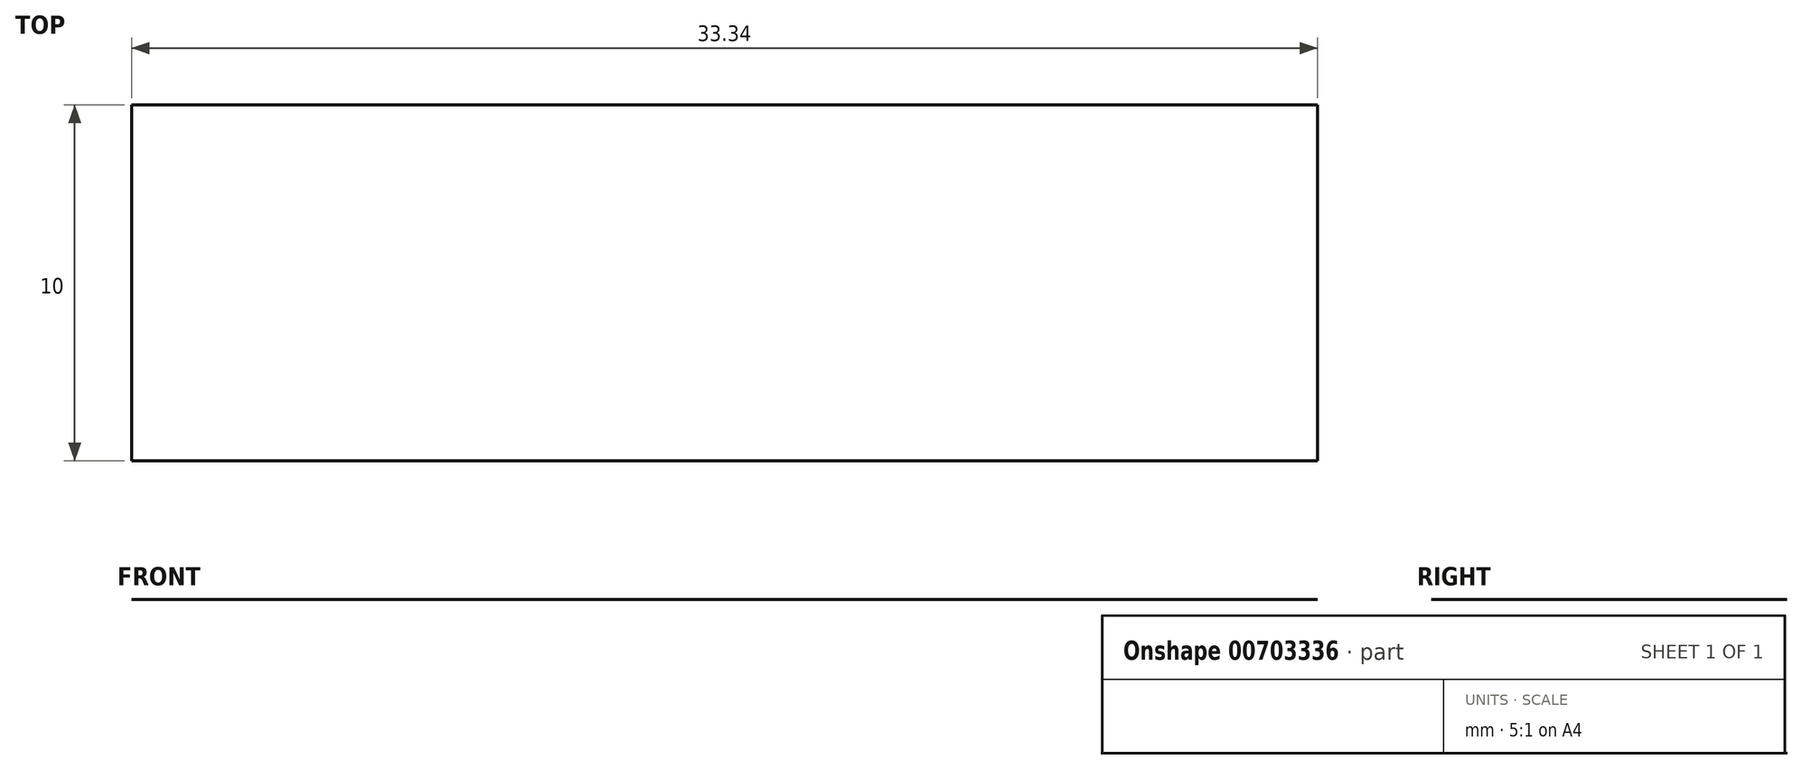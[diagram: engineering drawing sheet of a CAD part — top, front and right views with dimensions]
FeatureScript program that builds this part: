
annotation { "Feature Type Name" : "Feature", "Feature Type Description" : "" }
export const myFeature = defineFeature(function(context is Context, id is Id, definition is map)
    precondition{}
    {
        {
            var Q0;
            Q0=qCreatedBy(makeId("Top.planeOp"),FACE);
            var sketch = newSketch(context, id + "F0", { "sketchPlane" : qUnion([Q0])});
            skLineSegment(sketch, "E0.bottom", {"start": v(16.67, 5) * mm, "end": v(-16.67, 5) * mm});
            skLineSegment(sketch, "E0.top", {"start": v(16.67, -5) * mm, "end": v(-16.67, -5) * mm});
            skLineSegment(sketch, "E0.left", {"start": v(16.67, 5) * mm, "end": v(16.67, -5) * mm});
            skLineSegment(sketch, "E0.right", {"start": v(-16.67, 5) * mm, "end": v(-16.67, -5) * mm});
            skPoint(sketch, "E0.middle", {"position": v(0, 0) * mm});
            skSolve(sketch);
        }
        {
            var Q0;
            Q0 = qSketchRegion(id + "F0", true);
            extrude(context, id + "F1", {"entities" : qUnion([Q0]), "depth" : 1 / 406.4 * mm, "offsetDistance" : 25 * mm});
        }
    });
